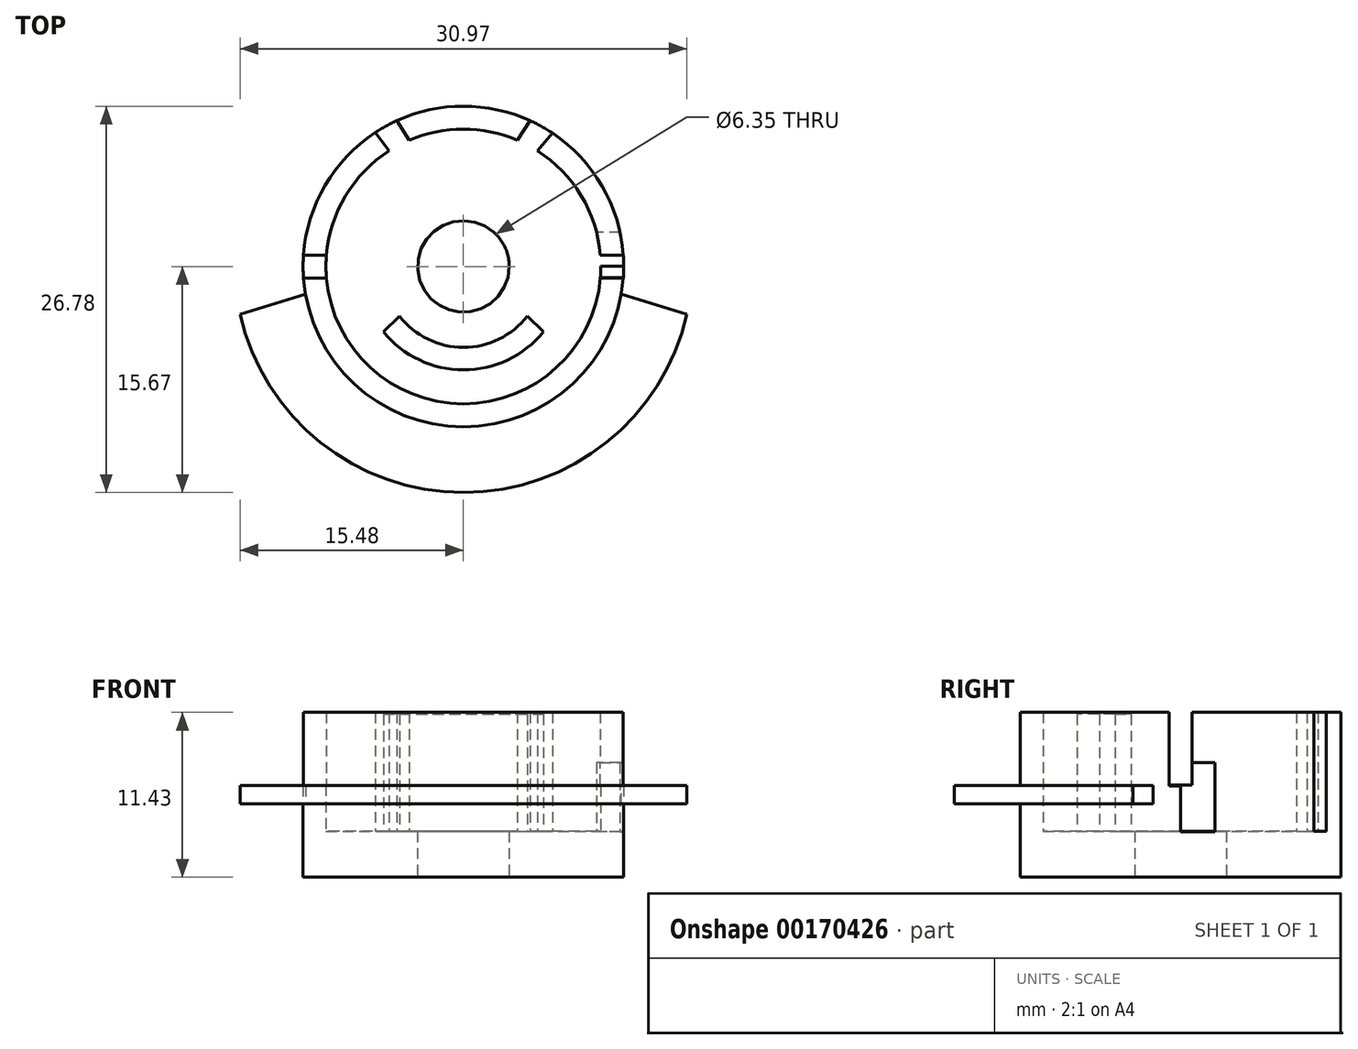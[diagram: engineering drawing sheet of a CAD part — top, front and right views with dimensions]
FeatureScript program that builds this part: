
annotation { "Feature Type Name" : "Feature", "Feature Type Description" : "" }
export const myFeature = defineFeature(function(context is Context, id is Id, definition is map)
    precondition{}
    {
        {
            var Q0;
            Q0=qCreatedBy(makeId("Top.planeOp"),FACE);
            var sketch = newSketch(context, id + "F0", { "sketchPlane" : qUnion([Q0])});
            skCircle(sketch, "E0", {"center": v(0, 0) * mm, "radius": 11.11 * mm});
            skSolve(sketch);
        }
        {
            var Q0;
            Q0 = qSketchRegion(id + "F0", true);
            extrude(context, id + "F1", {"entities" : qUnion([Q0]), "depth" : 3.17 * mm});
        }
        {
            var Q0;
            Q0=qCreatedBy(makeId("Top.planeOp"),FACE);
            var sketch = newSketch(context, id + "F2", { "sketchPlane" : qUnion([Q0])});
            skCircle(sketch, "E1", {"center": v(0, 0) * mm, "radius": 3.17 * mm});
            skSolve(sketch);
        }
        {
            var Q0;
            Q0 = qSketchRegion(id + "F2", true);
            extrude(context, id + "F3", {"entities" : qUnion([Q0]), "operationType" : NewBodyOperationType.REMOVE, "depth" : 71.12 * mm});
        }
        {
            var Q0;
            Q0=qCreatedBy(makeId("Top.planeOp"),FACE);
            cPlane(context, id + "F4", {"entities" : qUnion([Q0]), "cplaneType" : CPlaneType.OFFSET, "offset" : 3.17 * mm, "width" : 152.4 * mm, "height" : 152.4 * mm});
        }
        {
            var Q0;
            Q0=qCreatedBy(id+"F4.planeOp",FACE);
            var sketch = newSketch(context, id + "F5", { "sketchPlane" : qUnion([Q0])});
            skCircle(sketch, "E2", {"center": v(0, 0) * mm, "radius": 11.11 * mm});
            skSolve(sketch);
        }
        {
            var Q0;
            Q0 = qSketchRegion(id + "F5", true);
            extrude(context, id + "F6", {"entities" : qUnion([Q0]), "operationType" : NewBodyOperationType.ADD, "depth" : 8.25 * mm});
        }
        {
            var Q0;
            Q0=qCreatedBy(id+"F4.planeOp",FACE);
            var sketch = newSketch(context, id + "F7", { "sketchPlane" : qUnion([Q0])});
            skCircle(sketch, "E3", {"center": v(0, 0) * mm, "radius": 9.53 * mm});
            skSolve(sketch);
        }
        {
            var Q0;
            Q0 = qSketchRegion(id + "F7", true);
            extrude(context, id + "F8", {"entities" : qUnion([Q0]), "operationType" : NewBodyOperationType.REMOVE, "depth" : 25.4 * mm});
        }
        {
            var Q0;
            Q0=qCreatedBy(id+"F4.planeOp",FACE);
            cPlane(context, id + "F9", {"entities" : qUnion([Q0]), "cplaneType" : CPlaneType.OFFSET, "offset" : 3.17 * mm, "width" : 152.4 * mm, "height" : 152.4 * mm});
        }
        {
            var Q0;
            Q0=qCreatedBy(makeId("Right.planeOp"),FACE);
            var sketch = newSketch(context, id + "F10", { "sketchPlane" : qUnion([Q0])});
            skLineSegment(sketch, "E4", {"start": v(0, 6.4) * mm, "end": v(-0.8, 6.4) * mm});
            skLineSegment(sketch, "E5", {"start": v(0, 6.4) * mm, "end": v(0.8, 6.4) * mm});
            skLineSegment(sketch, "E6", {"start": v(-0.8, 6.4) * mm, "end": v(-0.8, 14.02) * mm});
            skLineSegment(sketch, "E7", {"start": v(0.8, 6.4) * mm, "end": v(0.8, 14.02) * mm});
            skLineSegment(sketch, "E8", {"start": v(0.8, 14.02) * mm, "end": v(-0.8, 14.02) * mm});
            skSolve(sketch);
        }
        {
            var Q0;
            Q0 = qSketchRegion(id + "F10", true);
            extrude(context, id + "F11", {"entities" : qUnion([Q0]), "operationType" : NewBodyOperationType.REMOVE, "oppositeDirection" : true, "depth" : 25.4 * mm, "hasSecondDirection" : true, "secondDirectionOppositeDirection" : false, "secondDirectionDepth" : 25.4 * mm});
        }
        {
            var Q0;
            Q0=qCreatedBy(makeId("Right.planeOp"),FACE);
            var sketch = newSketch(context, id + "F12", { "sketchPlane" : qUnion([Q0])});
            skLineSegment(sketch, "E9", {"start": v(-0.79, 7.95) * mm, "end": v(0.8, 7.95) * mm});
            skLineSegment(sketch, "E10", {"start": v(-0.79, 6.35) * mm, "end": v(-0.79, 7.95) * mm});
            skLineSegment(sketch, "E11", {"start": v(-0.79, 6.35) * mm, "end": v(0, 6.35) * mm});
            skPoint(sketch, "E12.start.orphan", {"position": v(0.8, 7.95) * mm});
            skPoint(sketch, "E13.endSnap0", {"position": v(0.8, 4.53) * mm});
            skPoint(sketch, "E14.orphan", {"position": v(0.8, 2.72) * mm});
            skPoint(sketch, "E15.orphan", {"position": v(2.38, 7.95) * mm});
            skLineSegment(sketch, "E16", {"start": v(0, 6.35) * mm, "end": v(0, 4.77) * mm});
            skPoint(sketch, "E17.start.orphan", {"position": v(0.8, 6.35) * mm});
            skPoint(sketch, "E18.start.orphan", {"position": v(0.8, 4.78) * mm});
            skLineSegment(sketch, "E19", {"start": v(0.8, 7.95) * mm, "end": v(2.38, 7.95) * mm});
            skLineSegment(sketch, "E20", {"start": v(2.38, 4.77) * mm, "end": v(2.38, 7.95) * mm});
            skLineSegment(sketch, "E21", {"start": v(0, 4.77) * mm, "end": v(0, 3.17) * mm});
            skLineSegment(sketch, "E22", {"start": v(2.38, 4.77) * mm, "end": v(2.38, 3.17) * mm});
            skLineSegment(sketch, "E23", {"start": v(2.38, 3.17) * mm, "end": v(0, 3.17) * mm});
            skSolve(sketch);
        }
        {
            var Q0;
            Q0 = qSketchRegion(id + "F12", true);
            extrude(context, id + "F13", {"entities" : qUnion([Q0]), "operationType" : NewBodyOperationType.REMOVE, "depth" : 25.4 * mm});
        }
        {
            var Q0;
            Q0=qCreatedBy(id+"F9.planeOp",FACE);
            var sketch = newSketch(context, id + "F14", { "sketchPlane" : qUnion([Q0])});
            skLineSegment(sketch, "E24", {"start": v(0, 0) * mm, "end": v(0, 11.18) * mm, "construction": true});
            skLineSegment(sketch, "E25", {"start": v(0, 11.18) * mm, "end": v(0, 8) * mm, "construction": true});
            skLineSegment(sketch, "E26", {"start": v(0, 8) * mm, "end": v(-5.06, 8) * mm, "construction": true});
            skLineSegment(sketch, "E27", {"start": v(0, 8) * mm, "end": v(4.84, 8) * mm, "construction": true});
            skLineSegment(sketch, "E28", {"start": v(5.11, 8) * mm, "end": v(6.3, 9.4) * mm});
            skLineSegment(sketch, "E29", {"start": v(5.11, 8) * mm, "end": v(3.72, 8.74) * mm});
            skLineSegment(sketch, "E30", {"start": v(3.72, 8.74) * mm, "end": v(4.7, 10.2) * mm});
            skLineSegment(sketch, "E31", {"start": v(4.7, 10.2) * mm, "end": v(6.3, 9.4) * mm});
            skLineSegment(sketch, "E32", {"start": v(-5.13, 8) * mm, "end": v(-6.22, 9.4) * mm});
            skLineSegment(sketch, "E33", {"start": v(-5.13, 8) * mm, "end": v(-3.73, 8.73) * mm});
            skLineSegment(sketch, "E34", {"start": v(-3.73, 8.73) * mm, "end": v(-4.7, 10.25) * mm});
            skLineSegment(sketch, "E35", {"start": v(-4.7, 10.25) * mm, "end": v(-6.22, 9.4) * mm});
            skSolve(sketch);
        }
        {
            var Q0;
            Q0 = qSketchRegion(id + "F14", true);
            extrude(context, id + "F15", {"entities" : qUnion([Q0]), "operationType" : NewBodyOperationType.REMOVE, "depth" : 25.4 * mm, "hasSecondDirection" : true, "secondDirectionOppositeDirection" : true, "secondDirectionDepth" : 3.17 * mm});
        }
        {
            var Q0;
            Q0=qCreatedBy(id+"F4.planeOp",FACE);
            var sketch = newSketch(context, id + "F16", { "sketchPlane" : qUnion([Q0])});
            skLineSegment(sketch, "E36", {"start": v(0, -7.18) * mm, "end": v(0, -7.17) * mm, "construction": true});
            skPoint(sketch, "E37.second.point", {"position": v(0, 15.02) * mm});
            skPoint(sketch, "E37.third.point", {"position": v(-11.08, 5.03) * mm});
            skArc(sketch, "E38", {"start": v(-5.55, -4.53) * mm, "mid": v(0, -7.17) * mm, "end": v(5.55, -4.53) * mm});
            skArc(sketch, "E39", {"start": v(-4.43, -3.44) * mm, "mid": v(0, -5.6) * mm, "end": v(4.43, -3.44) * mm});
            skLineSegment(sketch, "E40", {"start": v(5.55, -4.53) * mm, "end": v(4.43, -3.44) * mm});
            skLineSegment(sketch, "E41", {"start": v(-4.43, -3.44) * mm, "end": v(-5.55, -4.53) * mm});
            skLineSegment(sketch, "E42.trimOffspring", {"start": v(0, -5.6) * mm, "end": v(0, -5.6) * mm, "construction": true});
            skSolve(sketch);
        }
        {
            var Q0;
            Q0 = qSketchRegion(id + "F16", true);
            extrude(context, id + "F17", {"entities" : qUnion([Q0]), "operationType" : NewBodyOperationType.ADD, "depth" : 8.13 * mm});
        }
        {
            var Q0;
            Q0=qCreatedBy(makeId("Top.planeOp"),FACE);
            cPlane(context, id + "F18", {"entities" : qUnion([Q0]), "cplaneType" : CPlaneType.OFFSET, "offset" : 6.35 * mm, "width" : 152.4 * mm, "height" : 152.4 * mm});
        }
        {
            var Q0;
            Q0=qCreatedBy(id+"F18.planeOp",FACE);
            var sketch = newSketch(context, id + "F19", { "sketchPlane" : qUnion([Q0])});
            skLineSegment(sketch, "E43", {"start": v(10.94, -1.92) * mm, "end": v(15.5, -3.32) * mm});
            skLineSegment(sketch, "E44", {"start": v(-10.93, -1.92) * mm, "end": v(-15.48, -3.32) * mm});
            skArc(sketch, "E45", {"start": v(-15.48, -3.32) * mm, "mid": v(0, -15.67) * mm, "end": v(15.5, -3.32) * mm});
            skArc(sketch, "E46", {"start": v(-10.93, -1.92) * mm, "mid": v(0, -10.31) * mm, "end": v(10.94, -1.92) * mm});
            skSolve(sketch);
        }
        {
            var Q0;
            Q0 = qSketchRegion(id + "F19", true);
            extrude(context, id + "F20", {"entities" : qUnion([Q0]), "operationType" : NewBodyOperationType.ADD, "oppositeDirection" : true, "depth" : 1.27 * mm});
        }
    });
